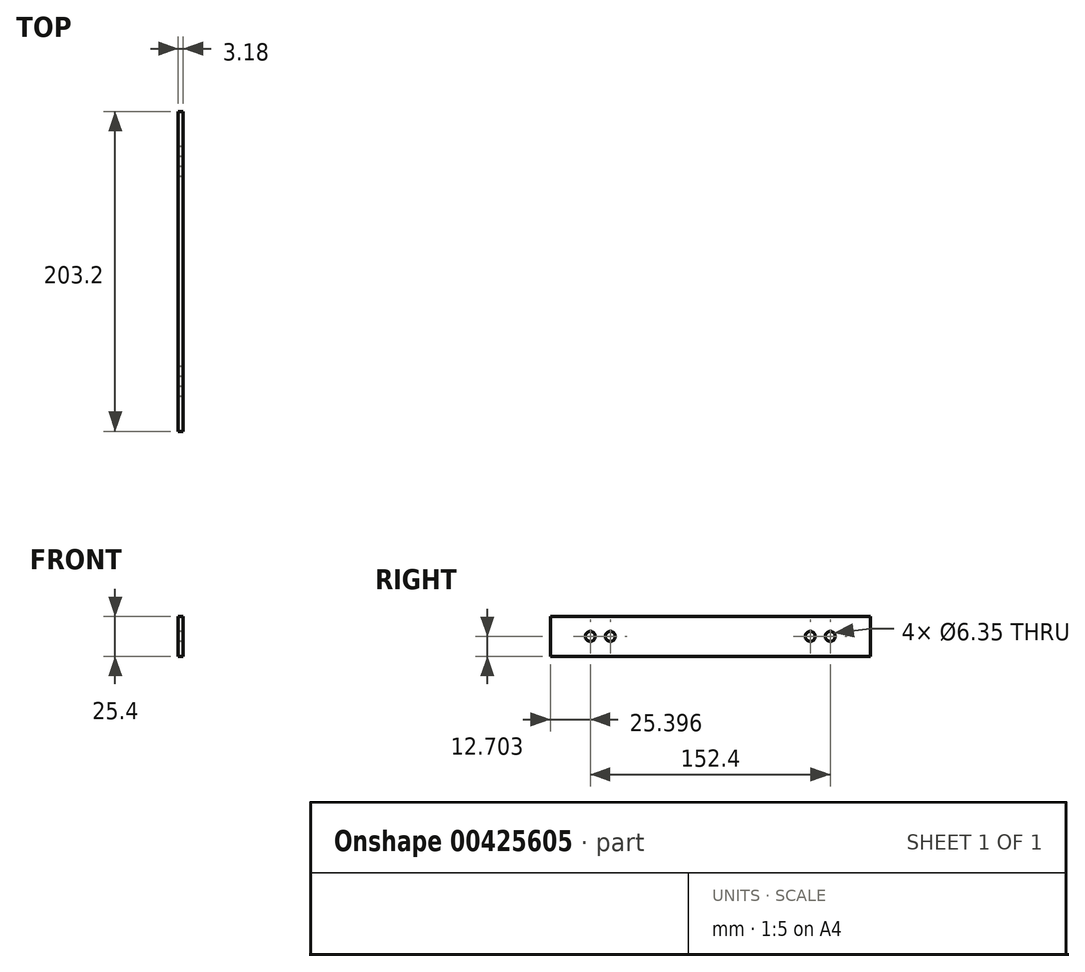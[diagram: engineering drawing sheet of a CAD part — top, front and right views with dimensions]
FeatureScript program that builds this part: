
annotation { "Feature Type Name" : "Feature", "Feature Type Description" : "" }
export const myFeature = defineFeature(function(context is Context, id is Id, definition is map)
    precondition{}
    {
        {
            var Q0;
            Q0=qCreatedBy(makeId("Right.planeOp"),FACE);
            var sketch = newSketch(context, id + "F0", { "sketchPlane" : qUnion([Q0])});
            skLineSegment(sketch, "E0.bottom", {"start": v(-95.15, -5.09) * mm, "end": v(108.05, -5.09) * mm});
            skLineSegment(sketch, "E0.top", {"start": v(-95.15, -30.49) * mm, "end": v(108.05, -30.49) * mm});
            skLineSegment(sketch, "E0.left", {"start": v(-95.15, -5.09) * mm, "end": v(-95.15, -30.49) * mm});
            skLineSegment(sketch, "E0.right", {"start": v(108.05, -5.09) * mm, "end": v(108.05, -30.49) * mm});
            skCircle(sketch, "E1", {"center": v(-69.75, -17.79) * mm, "radius": 3.18 * mm});
            skCircle(sketch, "E2", {"center": v(-57.05, -17.79) * mm, "radius": 3.18 * mm});
            skCircle(sketch, "E3", {"center": v(69.95, -17.79) * mm, "radius": 3.18 * mm});
            skCircle(sketch, "E4", {"center": v(82.65, -17.79) * mm, "radius": 3.18 * mm});
            skSolve(sketch);
        }
        {
            var Q0;
            Q0=makeQuery(id+"F0.imprint","IMPRINT",FACE,{"disambiguationData":[TD([[makeQuery(id+"F0.imprint","IMPRINT",EDGE,{"derivedFrom":sQuery(id+"F0.wireOp",EDGE,"E0.bottom")}),-1.0]])]});
            extrude(context, id + "F1", {"entities" : qUnion([Q0]), "depth" : 3.17 * mm});
        }
    });
